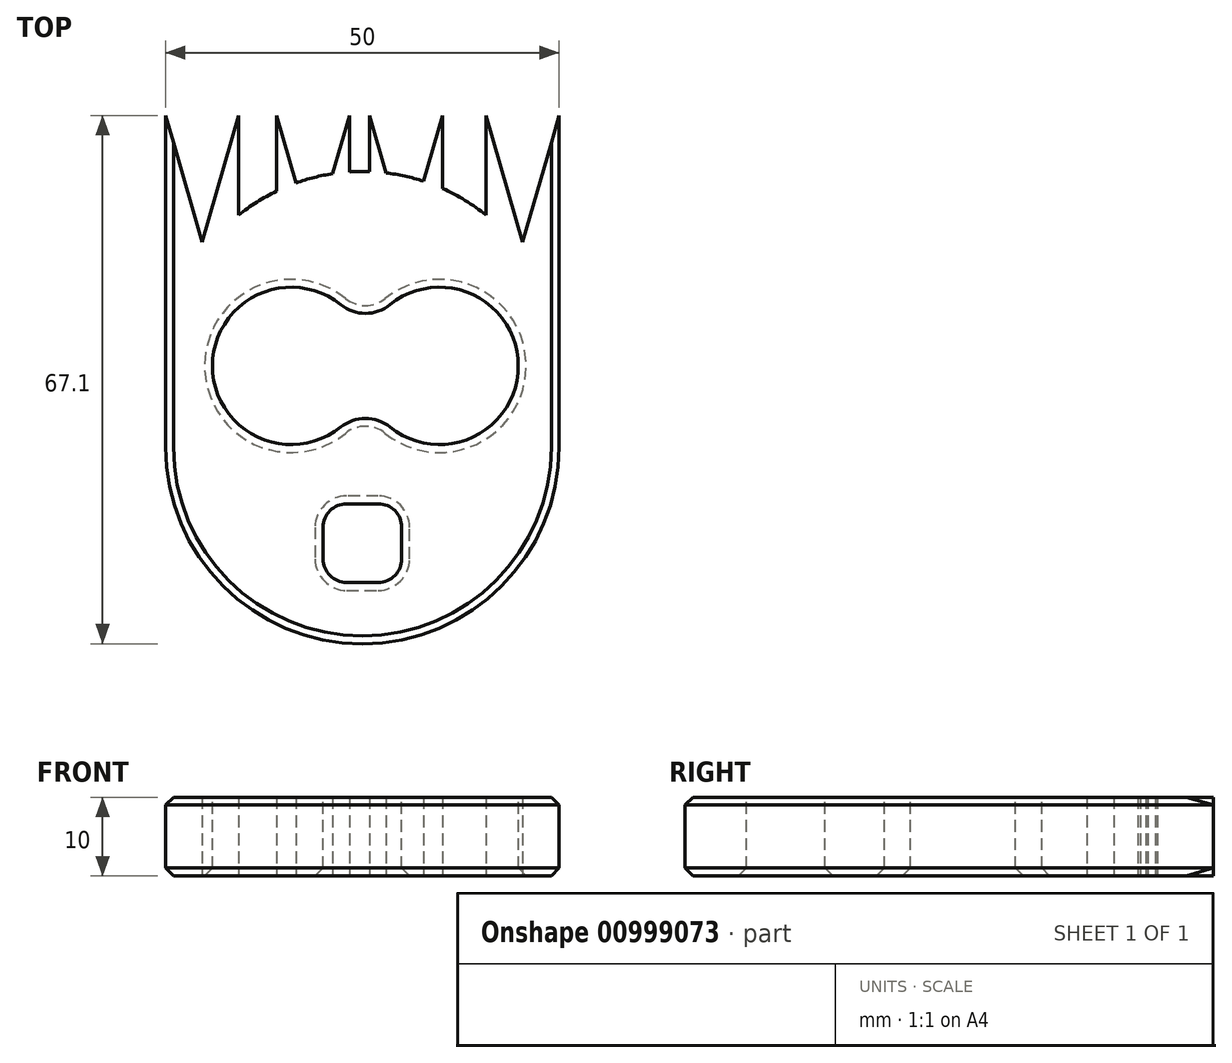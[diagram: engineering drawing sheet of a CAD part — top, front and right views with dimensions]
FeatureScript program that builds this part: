
annotation { "Feature Type Name" : "Feature", "Feature Type Description" : "" }
export const myFeature = defineFeature(function(context is Context, id is Id, definition is map)
    precondition{}
    {
        {
            var Q0;
            Q0=qCreatedBy(makeId("Top.planeOp"),FACE);
            var sketch = newSketch(context, id + "F0", { "sketchPlane" : qUnion([Q0])});
            skLineSegment(sketch, "E0.bottom", {"start": v(25, 5) * mm, "end": v(-25, 5) * mm});
            skLineSegment(sketch, "E0.top", {"start": v(25, -5) * mm, "end": v(-25, -5) * mm});
            skLineSegment(sketch, "E0.left", {"start": v(25, 5) * mm, "end": v(25, -5) * mm});
            skLineSegment(sketch, "E0.right", {"start": v(-25, 5) * mm, "end": v(-25, -5) * mm});
            skPoint(sketch, "E0.middle", {"position": v(0, 0) * mm});
            skArc(sketch, "E1", {"start": v(25, 5) * mm, "mid": v(0, 30) * mm, "end": v(-25, 5) * mm});
            skArc(sketch, "E2", {"start": v(-25, -5) * mm, "mid": v(0, -30) * mm, "end": v(25, -5) * mm});
            skLineSegment(sketch, "E3", {"start": v(-25, 5) * mm, "end": v(-25, 37.1) * mm});
            skLineSegment(sketch, "E4", {"start": v(-25, 37.1) * mm, "end": v(-15.73, 5) * mm});
            skLineSegment(sketch, "E5", {"start": v(-15.73, 5) * mm, "end": v(-15.73, 37.1) * mm});
            skLineSegment(sketch, "E6", {"start": v(-15.73, 37.1) * mm, "end": v(-25, 5) * mm});
            skLineSegment(sketch, "E7", {"start": v(-10.9, 5) * mm, "end": v(-10.9, 37.1) * mm});
            skLineSegment(sketch, "E8", {"start": v(-10.9, 37.1) * mm, "end": v(-1.64, 5) * mm});
            skLineSegment(sketch, "E9", {"start": v(-1.64, 5) * mm, "end": v(-1.64, 37.1) * mm});
            skLineSegment(sketch, "E10", {"start": v(-1.64, 37.1) * mm, "end": v(-10.9, 5) * mm});
            skLineSegment(sketch, "E11", {"start": v(0.9, 5) * mm, "end": v(0.9, 37.1) * mm});
            skLineSegment(sketch, "E12", {"start": v(0.9, 37.1) * mm, "end": v(10.16, 5) * mm});
            skLineSegment(sketch, "E13", {"start": v(10.16, 5) * mm, "end": v(10.16, 37.1) * mm});
            skLineSegment(sketch, "E14", {"start": v(10.16, 37.1) * mm, "end": v(0.9, 5) * mm});
            skLineSegment(sketch, "E15", {"start": v(25, 5) * mm, "end": v(25, 37.1) * mm});
            skLineSegment(sketch, "E16", {"start": v(25, 37.1) * mm, "end": v(15.73, 5) * mm});
            skLineSegment(sketch, "E17", {"start": v(15.73, 5) * mm, "end": v(15.73, 37.1) * mm});
            skLineSegment(sketch, "E18", {"start": v(15.73, 37.1) * mm, "end": v(25, 5) * mm});
            skSolve(sketch);
        }
        {
            var Q0;
            {var subQ0=sQuery(id+"F0.wireOp",EDGE,"E10");var subQ3=sQuery(id+"F0.wireOp",EDGE,"E8");var subQ5=makeQuery(id+"F0.imprint","INTERSECT",VERTEX,{"derivedFrom":[subQ3,subQ0]});Q0=makeQuery(id+"F0.imprint","IMPRINT",FACE,{"disambiguationData":[TD([[makeQuery(id+"F0.imprint","IMPRINT",EDGE,{"disambiguationData":[TD([[subQ5,-1.0]])],"derivedFrom":subQ3}),-1.0]])]});}
            var Q1;
            {var subQ0=sQuery(id+"F0.wireOp",EDGE,"E14");var subQ3=sQuery(id+"F0.wireOp",EDGE,"E12");var subQ5=makeQuery(id+"F0.imprint","INTERSECT",VERTEX,{"derivedFrom":[subQ3,subQ0]});Q1=makeQuery(id+"F0.imprint","IMPRINT",FACE,{"disambiguationData":[TD([[makeQuery(id+"F0.imprint","IMPRINT",EDGE,{"disambiguationData":[TD([[subQ5,-1.0]])],"derivedFrom":subQ3}),-1.0]])]});}
            var Q2;
            Q2=makeQuery(id+"F0.imprint","IMPRINT",FACE,{"disambiguationData":[TD([[makeQuery(id+"F0.imprint","IMPRINT",EDGE,{"derivedFrom":sQuery(id+"F0.wireOp",EDGE,"E0.top")}),1.0]])]});
            var Q3;
            {var subQ0=sQuery(id+"F0.wireOp",EDGE,"E13");var subQ1=sQuery(id+"F0.wireOp",EDGE,"E1");var subQ2=makeQuery(id+"F0.imprint","INTERSECT",VERTEX,{"derivedFrom":[subQ1,subQ0]});Q3=makeQuery(id+"F0.imprint","IMPRINT",FACE,{"disambiguationData":[TD([[makeQuery(id+"F0.imprint","IMPRINT",EDGE,{"disambiguationData":[TD([[subQ2,-1.0]])],"derivedFrom":subQ1}),-1.0]])]});}
            var Q4;
            {var subQ0=sQuery(id+"F0.wireOp",EDGE,"E12");var subQ1=sQuery(id+"F0.wireOp",EDGE,"E1");var subQ2=makeQuery(id+"F0.imprint","INTERSECT",VERTEX,{"derivedFrom":[subQ1,subQ0]});Q4=makeQuery(id+"F0.imprint","IMPRINT",FACE,{"disambiguationData":[TD([[makeQuery(id+"F0.imprint","IMPRINT",EDGE,{"disambiguationData":[TD([[subQ2,-1.0]])],"derivedFrom":subQ1}),-1.0]])]});}
            var Q5;
            {var subQ0=sQuery(id+"F0.wireOp",EDGE,"E9");var subQ1=sQuery(id+"F0.wireOp",EDGE,"E1");var subQ2=makeQuery(id+"F0.imprint","INTERSECT",VERTEX,{"derivedFrom":[subQ1,subQ0]});Q5=makeQuery(id+"F0.imprint","IMPRINT",FACE,{"disambiguationData":[TD([[makeQuery(id+"F0.imprint","IMPRINT",EDGE,{"disambiguationData":[TD([[subQ2,-1.0]])],"derivedFrom":subQ1}),-1.0]])]});}
            var Q6;
            {var subQ0=sQuery(id+"F0.wireOp",EDGE,"E8");var subQ1=sQuery(id+"F0.wireOp",EDGE,"E1");var subQ2=makeQuery(id+"F0.imprint","INTERSECT",VERTEX,{"derivedFrom":[subQ1,subQ0]});Q6=makeQuery(id+"F0.imprint","IMPRINT",FACE,{"disambiguationData":[TD([[makeQuery(id+"F0.imprint","IMPRINT",EDGE,{"disambiguationData":[TD([[subQ2,-1.0]])],"derivedFrom":subQ1}),-1.0]])]});}
            var Q7;
            {var subQ1=sQuery(id+"F0.wireOp",EDGE,"E15");Q7=makeQuery(id+"F0.imprint","IMPRINT",FACE,{"disambiguationData":[TD([[makeQuery(id+"F0.imprint","IMPRINT",EDGE,{"derivedFrom":subQ1}),1.0]])]});}
            var Q8;
            {var subQ0=sQuery(id+"F0.wireOp",EDGE,"E18");var subQ1=sQuery(id+"F0.wireOp",EDGE,"E1");var subQ3=makeQuery(id+"F0.imprint","INTERSECT",VERTEX,{"derivedFrom":[subQ1,subQ0]});Q8=makeQuery(id+"F0.imprint","IMPRINT",FACE,{"disambiguationData":[TD([[makeQuery(id+"F0.imprint","IMPRINT",EDGE,{"disambiguationData":[TD([[subQ3,1.0]])],"derivedFrom":subQ1}),1.0]])]});}
            var Q9;
            {var subQ0=sQuery(id+"F0.wireOp",EDGE,"E17");var subQ1=sQuery(id+"F0.wireOp",EDGE,"E1");var subQ2=makeQuery(id+"F0.imprint","INTERSECT",VERTEX,{"derivedFrom":[subQ1,subQ0]});Q9=makeQuery(id+"F0.imprint","IMPRINT",FACE,{"disambiguationData":[TD([[makeQuery(id+"F0.imprint","IMPRINT",EDGE,{"disambiguationData":[TD([[subQ2,1.0]])],"derivedFrom":subQ1}),-1.0]])]});}
            var Q10;
            {var subQ0=sQuery(id+"F0.wireOp",EDGE,"E14");var subQ1=sQuery(id+"F0.wireOp",EDGE,"E1");var subQ2=makeQuery(id+"F0.imprint","INTERSECT",VERTEX,{"derivedFrom":[subQ1,subQ0]});Q10=makeQuery(id+"F0.imprint","IMPRINT",FACE,{"disambiguationData":[TD([[makeQuery(id+"F0.imprint","IMPRINT",EDGE,{"disambiguationData":[TD([[subQ2,-1.0]])],"derivedFrom":subQ1}),1.0]])]});}
            var Q11;
            {var subQ0=sQuery(id+"F0.wireOp",EDGE,"E10");var subQ1=sQuery(id+"F0.wireOp",EDGE,"E1");var subQ2=makeQuery(id+"F0.imprint","INTERSECT",VERTEX,{"derivedFrom":[subQ1,subQ0]});Q11=makeQuery(id+"F0.imprint","IMPRINT",FACE,{"disambiguationData":[TD([[makeQuery(id+"F0.imprint","IMPRINT",EDGE,{"disambiguationData":[TD([[subQ2,-1.0]])],"derivedFrom":subQ1}),1.0]])]});}
            var Q12;
            {var subQ0=sQuery(id+"F0.wireOp",EDGE,"E5");var subQ1=sQuery(id+"F0.wireOp",EDGE,"E1");var subQ2=makeQuery(id+"F0.imprint","INTERSECT",VERTEX,{"derivedFrom":[subQ1,subQ0]});Q12=makeQuery(id+"F0.imprint","IMPRINT",FACE,{"disambiguationData":[TD([[makeQuery(id+"F0.imprint","IMPRINT",EDGE,{"disambiguationData":[TD([[subQ2,-1.0]])],"derivedFrom":subQ1}),-1.0]])]});}
            var Q13;
            {var subQ1=sQuery(id+"F0.wireOp",EDGE,"E3");Q13=makeQuery(id+"F0.imprint","IMPRINT",FACE,{"disambiguationData":[TD([[makeQuery(id+"F0.imprint","IMPRINT",EDGE,{"derivedFrom":subQ1}),-1.0]])]});}
            var Q14;
            {var subQ0=sQuery(id+"F0.wireOp",EDGE,"E6");var subQ1=sQuery(id+"F0.wireOp",EDGE,"E1");var subQ3=makeQuery(id+"F0.imprint","INTERSECT",VERTEX,{"derivedFrom":[subQ1,subQ0]});Q14=makeQuery(id+"F0.imprint","IMPRINT",FACE,{"disambiguationData":[TD([[makeQuery(id+"F0.imprint","IMPRINT",EDGE,{"disambiguationData":[TD([[subQ3,-1.0]])],"derivedFrom":subQ1}),1.0]])]});}
            var Q15;
            {var subQ3=sQuery(id+"F0.wireOp",EDGE,"E17");var subQ5=sQuery(id+"F0.wireOp",EDGE,"E1");var subQ6=makeQuery(id+"F0.imprint","INTERSECT",VERTEX,{"derivedFrom":[subQ5,subQ3]});Q15=makeQuery(id+"F0.imprint","IMPRINT",FACE,{"disambiguationData":[TD([[makeQuery(id+"F0.imprint","IMPRINT",EDGE,{"disambiguationData":[TD([[subQ6,-1.0]])],"derivedFrom":subQ5}),1.0]])]});}
            var Q16;
            {var subQ3=sQuery(id+"F0.wireOp",EDGE,"E11");var subQ5=sQuery(id+"F0.wireOp",EDGE,"E1");var subQ6=makeQuery(id+"F0.imprint","INTERSECT",VERTEX,{"derivedFrom":[subQ5,subQ3]});Q16=makeQuery(id+"F0.imprint","IMPRINT",FACE,{"disambiguationData":[TD([[makeQuery(id+"F0.imprint","IMPRINT",EDGE,{"disambiguationData":[TD([[subQ6,-1.0]])],"derivedFrom":subQ5}),1.0]])]});}
            var Q17;
            {var subQ3=sQuery(id+"F0.wireOp",EDGE,"E7");var subQ5=sQuery(id+"F0.wireOp",EDGE,"E1");var subQ7=makeQuery(id+"F0.imprint","INTERSECT",VERTEX,{"derivedFrom":[subQ5,subQ3]});Q17=makeQuery(id+"F0.imprint","IMPRINT",FACE,{"disambiguationData":[TD([[makeQuery(id+"F0.imprint","IMPRINT",EDGE,{"disambiguationData":[TD([[subQ7,-1.0]])],"derivedFrom":subQ5}),1.0]])]});}
            var Q18;
            {var subQ0=sQuery(id+"F0.wireOp",EDGE,"E18");var subQ1=sQuery(id+"F0.wireOp",EDGE,"E1");var subQ2=makeQuery(id+"F0.imprint","INTERSECT",VERTEX,{"derivedFrom":[subQ1,subQ0]});Q18=makeQuery(id+"F0.imprint","IMPRINT",FACE,{"disambiguationData":[TD([[makeQuery(id+"F0.imprint","IMPRINT",EDGE,{"disambiguationData":[TD([[subQ2,-1.0]])],"derivedFrom":subQ1}),-1.0]])]});}
            var Q19;
            {var subQ0=sQuery(id+"F0.wireOp",EDGE,"E17");var subQ1=sQuery(id+"F0.wireOp",EDGE,"E1");var subQ2=makeQuery(id+"F0.imprint","INTERSECT",VERTEX,{"derivedFrom":[subQ1,subQ0]});Q19=makeQuery(id+"F0.imprint","IMPRINT",FACE,{"disambiguationData":[TD([[makeQuery(id+"F0.imprint","IMPRINT",EDGE,{"disambiguationData":[TD([[subQ2,1.0]])],"derivedFrom":subQ1}),1.0]])]});}
            var Q20;
            {var subQ0=sQuery(id+"F0.wireOp",EDGE,"E5");var subQ1=sQuery(id+"F0.wireOp",EDGE,"E1");var subQ2=makeQuery(id+"F0.imprint","INTERSECT",VERTEX,{"derivedFrom":[subQ1,subQ0]});Q20=makeQuery(id+"F0.imprint","IMPRINT",FACE,{"disambiguationData":[TD([[makeQuery(id+"F0.imprint","IMPRINT",EDGE,{"disambiguationData":[TD([[subQ2,-1.0]])],"derivedFrom":subQ1}),1.0]])]});}
            var Q21;
            {var subQ0=sQuery(id+"F0.wireOp",EDGE,"E4");var subQ1=sQuery(id+"F0.wireOp",EDGE,"E1");var subQ2=makeQuery(id+"F0.imprint","INTERSECT",VERTEX,{"derivedFrom":[subQ1,subQ0]});Q21=makeQuery(id+"F0.imprint","IMPRINT",FACE,{"disambiguationData":[TD([[makeQuery(id+"F0.imprint","IMPRINT",EDGE,{"disambiguationData":[TD([[subQ2,-1.0]])],"derivedFrom":subQ1}),-1.0]])]});}
            var Q22;
            {var subQ0=sQuery(id+"F0.wireOp",EDGE,"E18");var subQ1=sQuery(id+"F0.wireOp",EDGE,"E1");var subQ6=makeQuery(id+"F0.imprint","INTERSECT",VERTEX,{"derivedFrom":[subQ1,subQ0]});Q22=makeQuery(id+"F0.imprint","IMPRINT",FACE,{"disambiguationData":[TD([[makeQuery(id+"F0.imprint","IMPRINT",EDGE,{"disambiguationData":[TD([[subQ6,-1.0]])],"derivedFrom":subQ1}),1.0]])]});}
            var Q23;
            {var subQ0=sQuery(id+"F0.wireOp",EDGE,"E13");var subQ1=sQuery(id+"F0.wireOp",EDGE,"E1");var subQ2=makeQuery(id+"F0.imprint","INTERSECT",VERTEX,{"derivedFrom":[subQ1,subQ0]});Q23=makeQuery(id+"F0.imprint","IMPRINT",FACE,{"disambiguationData":[TD([[makeQuery(id+"F0.imprint","IMPRINT",EDGE,{"disambiguationData":[TD([[subQ2,-1.0]])],"derivedFrom":subQ1}),1.0]])]});}
            var Q24;
            {var subQ0=sQuery(id+"F0.wireOp",EDGE,"E12");var subQ1=sQuery(id+"F0.wireOp",EDGE,"E1");var subQ2=makeQuery(id+"F0.imprint","INTERSECT",VERTEX,{"derivedFrom":[subQ1,subQ0]});Q24=makeQuery(id+"F0.imprint","IMPRINT",FACE,{"disambiguationData":[TD([[makeQuery(id+"F0.imprint","IMPRINT",EDGE,{"disambiguationData":[TD([[subQ2,-1.0]])],"derivedFrom":subQ1}),1.0]])]});}
            var Q25;
            {var subQ0=sQuery(id+"F0.wireOp",EDGE,"E9");var subQ1=sQuery(id+"F0.wireOp",EDGE,"E1");var subQ2=makeQuery(id+"F0.imprint","INTERSECT",VERTEX,{"derivedFrom":[subQ1,subQ0]});Q25=makeQuery(id+"F0.imprint","IMPRINT",FACE,{"disambiguationData":[TD([[makeQuery(id+"F0.imprint","IMPRINT",EDGE,{"disambiguationData":[TD([[subQ2,-1.0]])],"derivedFrom":subQ1}),1.0]])]});}
            var Q26;
            {var subQ0=sQuery(id+"F0.wireOp",EDGE,"E8");var subQ1=sQuery(id+"F0.wireOp",EDGE,"E1");var subQ2=makeQuery(id+"F0.imprint","INTERSECT",VERTEX,{"derivedFrom":[subQ1,subQ0]});Q26=makeQuery(id+"F0.imprint","IMPRINT",FACE,{"disambiguationData":[TD([[makeQuery(id+"F0.imprint","IMPRINT",EDGE,{"disambiguationData":[TD([[subQ2,-1.0]])],"derivedFrom":subQ1}),1.0]])]});}
            var Q27;
            Q27=makeQuery(id+"F0.imprint","IMPRINT",FACE,{"disambiguationData":[TD([[makeQuery(id+"F0.imprint","IMPRINT",EDGE,{"derivedFrom":sQuery(id+"F0.wireOp",EDGE,"E0.top")}),-1.0]])]});
            var Q28;
            {var subQ1=sQuery(id+"F0.wireOp",EDGE,"E1");var subQ4=sQuery(id+"F0.wireOp",EDGE,"E4");var subQ6=makeQuery(id+"F0.imprint","INTERSECT",VERTEX,{"derivedFrom":[subQ1,subQ4]});Q28=makeQuery(id+"F0.imprint","IMPRINT",FACE,{"disambiguationData":[TD([[makeQuery(id+"F0.imprint","IMPRINT",EDGE,{"disambiguationData":[TD([[subQ6,-1.0]])],"derivedFrom":subQ1}),1.0]])]});}
            extrude(context, id + "F1", {"entities" : qUnion([Q0, Q1, Q2, Q3, Q4, Q5, Q6, Q7, Q8, Q9, Q10, Q11, Q12, Q13, Q14, Q15, Q16, Q17, Q18, Q19, Q20, Q21, Q22, Q23, Q24, Q25, Q26, Q27, Q28]), "depth" : 10 * mm, "offsetDistance" : 25 * mm});
        }
        {
            var Q0;
            Q0=makeQuery(id+"F1.opExtrude","CAP_FACE",FACE,{"disambiguationData":[OSD([sQuery(id+"F0.wireOp",EDGE,"E0.left"),sQuery(id+"F0.wireOp",EDGE,"E0.right"),sQuery(id+"F0.wireOp",EDGE,"E1"),sQuery(id+"F0.wireOp",EDGE,"E2"),sQuery(id+"F0.wireOp",EDGE,"E3"),sQuery(id+"F0.wireOp",EDGE,"E4"),sQuery(id+"F0.wireOp",EDGE,"E5"),sQuery(id+"F0.wireOp",EDGE,"E6"),sQuery(id+"F0.wireOp",EDGE,"E7"),sQuery(id+"F0.wireOp",EDGE,"E8"),sQuery(id+"F0.wireOp",EDGE,"E9"),sQuery(id+"F0.wireOp",EDGE,"E10"),sQuery(id+"F0.wireOp",EDGE,"E11"),sQuery(id+"F0.wireOp",EDGE,"E12"),sQuery(id+"F0.wireOp",EDGE,"E13"),sQuery(id+"F0.wireOp",EDGE,"E14"),sQuery(id+"F0.wireOp",EDGE,"E15"),sQuery(id+"F0.wireOp",EDGE,"E16"),sQuery(id+"F0.wireOp",EDGE,"E17"),sQuery(id+"F0.wireOp",EDGE,"E18")])],"isStart":false});
            var sketch = newSketch(context, id + "F2", { "sketchPlane" : qUnion([Q0])});
            skCircle(sketch, "E19", {"center": v(-9.04, 5.3) * mm, "radius": 10 * mm});
            skCircle(sketch, "E20", {"center": v(9.8, 5.3) * mm, "radius": 10 * mm});
            skSolve(sketch);
        }
        {
            var Q0;
            Q0 = qSketchRegion(id + "F2", true);
            extrude(context, id + "F3", {"entities" : qUnion([Q0]), "operationType" : NewBodyOperationType.REMOVE, "oppositeDirection" : true, "depth" : 25 * mm, "offsetDistance" : 25 * mm});
        }
        {
            var Q0;
            {var subQ0=sQuery(id+"F2.wireOp",EDGE,"E20");var subQ1=sQuery(id+"F2.wireOp",EDGE,"E19");Q0=makeQuery(id+"F3.boolean.opBoolean","COPY",EDGE,{"derivedFrom":makeQuery(id+"F3.opExtrude","SWEPT_EDGE",EDGE,{"disambiguationData":[OSD([subQ1,subQ0]),TDD([makeQuery(id+"F2.imprint","INTERSECT",VERTEX,{"disambiguationData":[OD(0.0)],"derivedFrom":[subQ1,subQ0]})])]})});}
            var Q1;
            {var subQ0=sQuery(id+"F2.wireOp",EDGE,"E20");var subQ1=sQuery(id+"F2.wireOp",EDGE,"E19");Q1=makeQuery(id+"F3.boolean.opBoolean","COPY",EDGE,{"derivedFrom":makeQuery(id+"F3.opExtrude","SWEPT_EDGE",EDGE,{"disambiguationData":[OSD([subQ1,subQ0]),TDD([makeQuery(id+"F2.imprint","INTERSECT",VERTEX,{"disambiguationData":[OD(1.0)],"derivedFrom":[subQ1,subQ0]})])]})});}
            fillet(context, id + "F4", {"entities" : qUnion([Q0, Q1]), "radius" : 5 * mm, "tangentPropagation" : true, "allowEdgeOverflow" : false});
        }
        {
            var Q0;
            Q0=makeQuery(id+"F1.opExtrude","CAP_FACE",FACE,{"disambiguationData":[OSD([sQuery(id+"F0.wireOp",EDGE,"E0.left"),sQuery(id+"F0.wireOp",EDGE,"E0.right"),sQuery(id+"F0.wireOp",EDGE,"E1"),sQuery(id+"F0.wireOp",EDGE,"E2"),sQuery(id+"F0.wireOp",EDGE,"E3"),sQuery(id+"F0.wireOp",EDGE,"E4"),sQuery(id+"F0.wireOp",EDGE,"E5"),sQuery(id+"F0.wireOp",EDGE,"E6"),sQuery(id+"F0.wireOp",EDGE,"E7"),sQuery(id+"F0.wireOp",EDGE,"E8"),sQuery(id+"F0.wireOp",EDGE,"E9"),sQuery(id+"F0.wireOp",EDGE,"E10"),sQuery(id+"F0.wireOp",EDGE,"E11"),sQuery(id+"F0.wireOp",EDGE,"E12"),sQuery(id+"F0.wireOp",EDGE,"E13"),sQuery(id+"F0.wireOp",EDGE,"E14"),sQuery(id+"F0.wireOp",EDGE,"E15"),sQuery(id+"F0.wireOp",EDGE,"E16"),sQuery(id+"F0.wireOp",EDGE,"E17"),sQuery(id+"F0.wireOp",EDGE,"E18")])],"isStart":false});
            var sketch = newSketch(context, id + "F5", { "sketchPlane" : qUnion([Q0])});
            skLineSegment(sketch, "E21.bottom", {"start": v(-5, -22.22) * mm, "end": v(5, -22.22) * mm});
            skLineSegment(sketch, "E21.top", {"start": v(-5, -12.22) * mm, "end": v(5, -12.22) * mm});
            skLineSegment(sketch, "E21.left", {"start": v(-5, -22.22) * mm, "end": v(-5, -12.22) * mm});
            skLineSegment(sketch, "E21.right", {"start": v(5, -22.22) * mm, "end": v(5, -12.22) * mm});
            skPoint(sketch, "E21.middle", {"position": v(0, -17.22) * mm});
            skSolve(sketch);
        }
        {
            var Q0;
            Q0=makeQuery(id+"F5.imprint","IMPRINT",FACE,{"disambiguationData":[TD([[makeQuery(id+"F5.imprint","IMPRINT",EDGE,{"derivedFrom":sQuery(id+"F5.wireOp",EDGE,"E21.bottom")}),1.0]])]});
            extrude(context, id + "F6", {"entities" : qUnion([Q0]), "operationType" : NewBodyOperationType.REMOVE, "oppositeDirection" : true, "depth" : 25 * mm, "offsetDistance" : 25 * mm});
        }
        {
            var Q0;
            Q0=makeQuery(id+"F6.boolean.opBoolean","COPY",EDGE,{"derivedFrom":makeQuery(id+"F6.opExtrude","SWEPT_EDGE",EDGE,{"disambiguationData":[OSD([sQuery(id+"F5.wireOp",EDGE,"E21.bottom"),sQuery(id+"F5.wireOp",EDGE,"E21.left")])]})});
            var Q1;
            Q1=makeQuery(id+"F6.boolean.opBoolean","COPY",EDGE,{"derivedFrom":makeQuery(id+"F6.opExtrude","SWEPT_EDGE",EDGE,{"disambiguationData":[OSD([sQuery(id+"F5.wireOp",EDGE,"E21.top"),sQuery(id+"F5.wireOp",EDGE,"E21.left")])]})});
            var Q2;
            Q2=makeQuery(id+"F6.boolean.opBoolean","COPY",EDGE,{"derivedFrom":makeQuery(id+"F6.opExtrude","SWEPT_EDGE",EDGE,{"disambiguationData":[OSD([sQuery(id+"F5.wireOp",EDGE,"E21.top"),sQuery(id+"F5.wireOp",EDGE,"E21.right")])]})});
            var Q3;
            Q3=makeQuery(id+"F6.boolean.opBoolean","COPY",EDGE,{"derivedFrom":makeQuery(id+"F6.opExtrude","SWEPT_EDGE",EDGE,{"disambiguationData":[OSD([sQuery(id+"F5.wireOp",EDGE,"E21.bottom"),sQuery(id+"F5.wireOp",EDGE,"E21.right")])]})});
            fillet(context, id + "F7", {"entities" : qUnion([Q0, Q1, Q2, Q3]), "radius" : 3 * mm, "tangentPropagation" : true, "allowEdgeOverflow" : false});
        }
        {
            var Q0;
            Q0=makeQuery(id+"F1.opExtrude","CAP_EDGE",EDGE,{"disambiguationData":[OSD([sQuery(id+"F0.wireOp",EDGE,"E2")])],"isStart":false});
            var Q1;
            Q1=makeQuery(id+"F1.opExtrude","CAP_EDGE",EDGE,{"disambiguationData":[OSD([sQuery(id+"F0.wireOp",EDGE,"E2")])],"isStart":true});
            var Q2;
            Q2=makeQuery(id+"F3.boolean.opBoolean","COPY",EDGE,{"derivedFrom":makeQuery(id+"F3.opExtrude","CAP_EDGE",EDGE,{"disambiguationData":[OSD([sQuery(id+"F2.wireOp",EDGE,"E19")])],"isStart":true})});
            var Q3;
            Q3=makeQuery(id+"F6.boolean.opBoolean","COPY",EDGE,{"derivedFrom":makeQuery(id+"F6.opExtrude","CAP_EDGE",EDGE,{"disambiguationData":[OSD([sQuery(id+"F5.wireOp",EDGE,"E21.top")])],"isStart":true})});
            var Q4;
            Q4=makeQuery(id+"F6.boolean.opBoolean","INTERSECT",EDGE,{"derivedFrom":[makeQuery(id+"F1.opExtrude","CAP_FACE",FACE,{"disambiguationData":[OSD([sQuery(id+"F0.wireOp",EDGE,"E0.left"),sQuery(id+"F0.wireOp",EDGE,"E0.right"),sQuery(id+"F0.wireOp",EDGE,"E1"),sQuery(id+"F0.wireOp",EDGE,"E2"),sQuery(id+"F0.wireOp",EDGE,"E3"),sQuery(id+"F0.wireOp",EDGE,"E4"),sQuery(id+"F0.wireOp",EDGE,"E5"),sQuery(id+"F0.wireOp",EDGE,"E6"),sQuery(id+"F0.wireOp",EDGE,"E7"),sQuery(id+"F0.wireOp",EDGE,"E8"),sQuery(id+"F0.wireOp",EDGE,"E9"),sQuery(id+"F0.wireOp",EDGE,"E10"),sQuery(id+"F0.wireOp",EDGE,"E11"),sQuery(id+"F0.wireOp",EDGE,"E12"),sQuery(id+"F0.wireOp",EDGE,"E13"),sQuery(id+"F0.wireOp",EDGE,"E14"),sQuery(id+"F0.wireOp",EDGE,"E15"),sQuery(id+"F0.wireOp",EDGE,"E16"),sQuery(id+"F0.wireOp",EDGE,"E17"),sQuery(id+"F0.wireOp",EDGE,"E18")])],"isStart":true}),makeQuery(id+"F6.opExtrude","SWEPT_FACE",FACE,{"disambiguationData":[OSD([sQuery(id+"F5.wireOp",EDGE,"E21.bottom")])]})]});
            var Q5;
            {var subQ0=sQuery(id+"F2.wireOp",EDGE,"E20");var subQ1=sQuery(id+"F2.wireOp",EDGE,"E19");Q5=makeQuery(id+"F4.opFillet","BLEND_EDGE",EDGE,{"blendedFrom":[makeQuery(id+"F3.boolean.opBoolean","COPY",EDGE,{"derivedFrom":makeQuery(id+"F3.opExtrude","SWEPT_EDGE",EDGE,{"disambiguationData":[OSD([subQ1,subQ0]),TDD([makeQuery(id+"F2.imprint","INTERSECT",VERTEX,{"disambiguationData":[OD(1.0)],"derivedFrom":[subQ1,subQ0]})])]})}),makeQuery(id+"F1.opExtrude","CAP_FACE",FACE,{"disambiguationData":[OSD([sQuery(id+"F0.wireOp",EDGE,"E0.left"),sQuery(id+"F0.wireOp",EDGE,"E0.right"),sQuery(id+"F0.wireOp",EDGE,"E1"),sQuery(id+"F0.wireOp",EDGE,"E2"),sQuery(id+"F0.wireOp",EDGE,"E3"),sQuery(id+"F0.wireOp",EDGE,"E4"),sQuery(id+"F0.wireOp",EDGE,"E5"),sQuery(id+"F0.wireOp",EDGE,"E6"),sQuery(id+"F0.wireOp",EDGE,"E7"),sQuery(id+"F0.wireOp",EDGE,"E8"),sQuery(id+"F0.wireOp",EDGE,"E9"),sQuery(id+"F0.wireOp",EDGE,"E10"),sQuery(id+"F0.wireOp",EDGE,"E11"),sQuery(id+"F0.wireOp",EDGE,"E12"),sQuery(id+"F0.wireOp",EDGE,"E13"),sQuery(id+"F0.wireOp",EDGE,"E14"),sQuery(id+"F0.wireOp",EDGE,"E15"),sQuery(id+"F0.wireOp",EDGE,"E16"),sQuery(id+"F0.wireOp",EDGE,"E17"),sQuery(id+"F0.wireOp",EDGE,"E18")])],"isStart":true})],"blendedInto":[makeQuery(id+"F1.opExtrude","CAP_FACE",FACE,{"disambiguationData":[OSD([sQuery(id+"F0.wireOp",EDGE,"E0.left"),sQuery(id+"F0.wireOp",EDGE,"E0.right"),sQuery(id+"F0.wireOp",EDGE,"E1"),sQuery(id+"F0.wireOp",EDGE,"E2"),sQuery(id+"F0.wireOp",EDGE,"E3"),sQuery(id+"F0.wireOp",EDGE,"E4"),sQuery(id+"F0.wireOp",EDGE,"E5"),sQuery(id+"F0.wireOp",EDGE,"E6"),sQuery(id+"F0.wireOp",EDGE,"E7"),sQuery(id+"F0.wireOp",EDGE,"E8"),sQuery(id+"F0.wireOp",EDGE,"E9"),sQuery(id+"F0.wireOp",EDGE,"E10"),sQuery(id+"F0.wireOp",EDGE,"E11"),sQuery(id+"F0.wireOp",EDGE,"E12"),sQuery(id+"F0.wireOp",EDGE,"E13"),sQuery(id+"F0.wireOp",EDGE,"E14"),sQuery(id+"F0.wireOp",EDGE,"E15"),sQuery(id+"F0.wireOp",EDGE,"E16"),sQuery(id+"F0.wireOp",EDGE,"E17"),sQuery(id+"F0.wireOp",EDGE,"E18")])],"isStart":true})]});}
            chamfer(context, id + "F8", {"entities" : qUnion([Q0, Q1, Q2, Q3, Q4, Q5]), "width" : 1 * mm, "tangentPropagation" : true});
        }
    });
